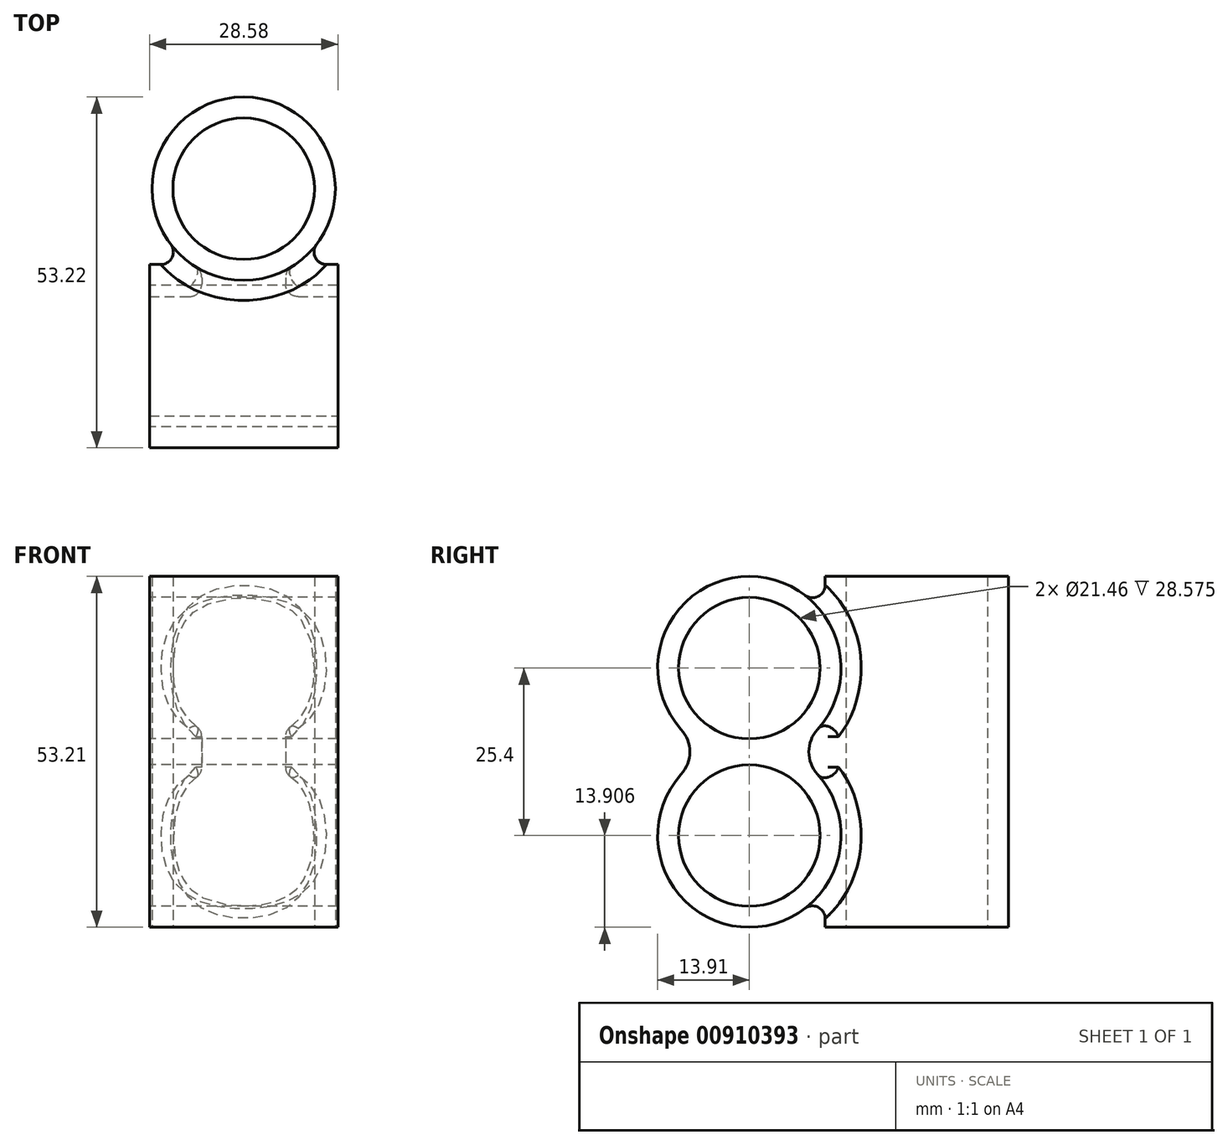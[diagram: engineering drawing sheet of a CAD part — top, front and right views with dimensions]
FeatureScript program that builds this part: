
annotation { "Feature Type Name" : "Feature", "Feature Type Description" : "" }
export const myFeature = defineFeature(function(context is Context, id is Id, definition is map)
    precondition{}
    {
        {
            var Q0;
            Q0=qCreatedBy(makeId("Top.planeOp"),FACE);
            var sketch = newSketch(context, id + "F0", { "sketchPlane" : qUnion([Q0])});
            skCircle(sketch, "E0", {"center": v(0, 0) * mm, "radius": 13.9 * mm});
            skCircle(sketch, "E1", {"center": v(0, 0) * mm, "radius": 10.73 * mm});
            skSolve(sketch);
        }
        {
            var Q0;
            Q0 = qSketchRegion(id + "F0", true);
            extrude(context, id + "F1", {"entities" : qUnion([Q0]), "depth" : 53.2 * mm, "offsetDistance" : 25.4 * mm});
        }
        {
            var Q0;
            Q0=qCreatedBy(makeId("Right.planeOp"),FACE);
            var sketch = newSketch(context, id + "F2", { "sketchPlane" : qUnion([Q0])});
            skCircle(sketch, "E2", {"center": v(-25.4, 13.9) * mm, "radius": 10.73 * mm});
            skCircle(sketch, "E3", {"center": v(-25.4, 39.3) * mm, "radius": 10.73 * mm});
            skArc(sketch, "E4", {"start": v(-31.07, 26.6) * mm, "mid": v(-25.4, 0) * mm, "end": v(-19.73, 26.6) * mm});
            skArc(sketch, "E5", {"start": v(-19.73, 26.6) * mm, "mid": v(-25.4, 53.21) * mm, "end": v(-31.07, 26.6) * mm});
            skSolve(sketch);
        }
        {
            var Q0;
            Q0 = qSketchRegion(id + "F2", true);
            extrude(context, id + "F3", {"entities" : qUnion([Q0]), "operationType" : NewBodyOperationType.ADD, "depth" : 28.57 * mm, "offsetDistance" : 25.4 * mm, "symmetric" : true});
        }
        {
            var Q0;
            {var subQ0=sQuery(id+"F2.wireOp",EDGE,"E5");var subQ1=sQuery(id+"F2.wireOp",EDGE,"E4");Q0=makeQuery(id+"F3.opExtrude","SWEPT_EDGE",EDGE,{"disambiguationData":[OSD([subQ1,subQ0]),TDD([makeQuery(id+"F2.imprint","INTERSECT",VERTEX,{"disambiguationData":[OD(0.0)],"derivedFrom":[subQ1,subQ0]})])]});}
            fillet(context, id + "F4", {"entities" : qUnion([Q0]), "radius" : 5.08 * mm, "tangentPropagation" : true, "allowEdgeOverflow" : false});
        }
        {
            var Q0;
            Q0=qCreatedBy(makeId("Right.planeOp"),FACE);
            var sketch = newSketch(context, id + "F5", { "sketchPlane" : qUnion([Q0])});
            skLineSegment(sketch, "E6", {"start": v(-19.73, 26.6) * mm, "end": v(-11.5, 13.9) * mm});
            skLineSegment(sketch, "E7", {"start": v(-11.5, 13.9) * mm, "end": v(-11.5, 39.3) * mm});
            skLineSegment(sketch, "E8", {"start": v(-11.5, 39.3) * mm, "end": v(-19.73, 26.6) * mm});
            skSolve(sketch);
        }
        {
            var Q0;
            Q0 = qSketchRegion(id + "F5", true);
            extrude(context, id + "F6", {"entities" : qUnion([Q0]), "operationType" : NewBodyOperationType.ADD, "depth" : 12.7 * mm, "offsetDistance" : 25.4 * mm, "symmetric" : true});
        }
        {
            var Q0;
            {var subQ0=sQuery(id+"F2.wireOp",EDGE,"E5");var subQ1=sQuery(id+"F2.wireOp",EDGE,"E4");Q0=makeQuery(id+"F6.boolean.opBoolean","SPLIT",EDGE,{"disambiguationData":[TD([makeQuery(id+"F6.opExtrude","CAP_FACE",FACE,{"disambiguationData":[OSD([sQuery(id+"F5.wireOp",EDGE,"E6"),sQuery(id+"F5.wireOp",EDGE,"E7"),sQuery(id+"F5.wireOp",EDGE,"E8")])],"isStart":false})])],"derivedFrom":makeQuery(id+"F3.opExtrude","SWEPT_EDGE",EDGE,{"disambiguationData":[OSD([subQ1,subQ0]),TDD([makeQuery(id+"F2.imprint","INTERSECT",VERTEX,{"disambiguationData":[OD(1.0)],"derivedFrom":[subQ1,subQ0]})])]})});}
            var Q1;
            {var subQ0=sQuery(id+"F2.wireOp",EDGE,"E5");var subQ1=sQuery(id+"F2.wireOp",EDGE,"E4");Q1=makeQuery(id+"F6.boolean.opBoolean","SPLIT",EDGE,{"disambiguationData":[TD([makeQuery(id+"F6.opExtrude","CAP_FACE",FACE,{"disambiguationData":[OSD([sQuery(id+"F5.wireOp",EDGE,"E6"),sQuery(id+"F5.wireOp",EDGE,"E7"),sQuery(id+"F5.wireOp",EDGE,"E8")])],"isStart":true})])],"derivedFrom":makeQuery(id+"F3.opExtrude","SWEPT_EDGE",EDGE,{"disambiguationData":[OSD([subQ1,subQ0]),TDD([makeQuery(id+"F2.imprint","INTERSECT",VERTEX,{"disambiguationData":[OD(1.0)],"derivedFrom":[subQ1,subQ0]})])]})});}
            fillet(context, id + "F7", {"entities" : qUnion([Q0, Q1]), "radius" : 5.08 * mm, "tangentPropagation" : true, "allowEdgeOverflow" : false});
        }
        {
            var Q0;
            Q0=makeQuery(id+"F3.boolean.opBoolean","INTERSECT",EDGE,{"derivedFrom":[makeQuery(id+"F1.opExtrude","SWEPT_FACE",FACE,{"disambiguationData":[OSD([sQuery(id+"F0.wireOp",EDGE,"E0")])]}),makeQuery(id+"F3.opExtrude","SWEPT_FACE",FACE,{"disambiguationData":[OSD([sQuery(id+"F2.wireOp",EDGE,"E4")])]})]});
            var Q1;
            Q1=makeQuery(id+"F3.boolean.opBoolean","INTERSECT",EDGE,{"derivedFrom":[makeQuery(id+"F1.opExtrude","SWEPT_FACE",FACE,{"disambiguationData":[OSD([sQuery(id+"F0.wireOp",EDGE,"E0")])]}),makeQuery(id+"F3.opExtrude","SWEPT_FACE",FACE,{"disambiguationData":[OSD([sQuery(id+"F2.wireOp",EDGE,"E5")])]})]});
            var Q2;
            {var subQ0=makeQuery(id+"F6.opExtrude","CAP_FACE",FACE,{"disambiguationData":[OSD([sQuery(id+"F5.wireOp",EDGE,"E6"),sQuery(id+"F5.wireOp",EDGE,"E7"),sQuery(id+"F5.wireOp",EDGE,"E8")])],"isStart":false});var subQ1=sQuery(id+"F2.wireOp",EDGE,"E5");var subQ2=sQuery(id+"F2.wireOp",EDGE,"E4");Q2=makeQuery(id+"F7.opFillet","BLEND_EDGE",EDGE,{"blendedFrom":[makeQuery(id+"F6.boolean.opBoolean","SPLIT",EDGE,{"disambiguationData":[TD([subQ0])],"derivedFrom":makeQuery(id+"F3.opExtrude","SWEPT_EDGE",EDGE,{"disambiguationData":[OSD([subQ2,subQ1]),TDD([makeQuery(id+"F2.imprint","INTERSECT",VERTEX,{"disambiguationData":[OD(1.0)],"derivedFrom":[subQ2,subQ1]})])]})}),subQ0],"blendedInto":[subQ0]});}
            var Q3;
            Q3=makeQuery(id+"F6.boolean.opBoolean","INTERSECT",EDGE,{"derivedFrom":[makeQuery(id+"F3.opExtrude","SWEPT_FACE",FACE,{"disambiguationData":[OSD([sQuery(id+"F2.wireOp",EDGE,"E5")])]}),makeQuery(id+"F6.opExtrude","CAP_FACE",FACE,{"disambiguationData":[OSD([sQuery(id+"F5.wireOp",EDGE,"E6"),sQuery(id+"F5.wireOp",EDGE,"E7"),sQuery(id+"F5.wireOp",EDGE,"E8")])],"isStart":false})]});
            var Q4;
            Q4=makeQuery(id+"F6.boolean.opBoolean","INTERSECT",EDGE,{"derivedFrom":[makeQuery(id+"F3.opExtrude","SWEPT_FACE",FACE,{"disambiguationData":[OSD([sQuery(id+"F2.wireOp",EDGE,"E4")])]}),makeQuery(id+"F6.opExtrude","CAP_FACE",FACE,{"disambiguationData":[OSD([sQuery(id+"F5.wireOp",EDGE,"E6"),sQuery(id+"F5.wireOp",EDGE,"E7"),sQuery(id+"F5.wireOp",EDGE,"E8")])],"isStart":false})]});
            var Q5;
            Q5=makeQuery(id+"F6.boolean.opBoolean","INTERSECT",EDGE,{"derivedFrom":[makeQuery(id+"F1.opExtrude","SWEPT_FACE",FACE,{"disambiguationData":[OSD([sQuery(id+"F0.wireOp",EDGE,"E0")])]}),makeQuery(id+"F6.opExtrude","CAP_FACE",FACE,{"disambiguationData":[OSD([sQuery(id+"F5.wireOp",EDGE,"E6"),sQuery(id+"F5.wireOp",EDGE,"E7"),sQuery(id+"F5.wireOp",EDGE,"E8")])],"isStart":false})]});
            var Q6;
            Q6=makeQuery(id+"F6.boolean.opBoolean","INTERSECT",EDGE,{"derivedFrom":[makeQuery(id+"F1.opExtrude","SWEPT_FACE",FACE,{"disambiguationData":[OSD([sQuery(id+"F0.wireOp",EDGE,"E0")])]}),makeQuery(id+"F6.opExtrude","CAP_FACE",FACE,{"disambiguationData":[OSD([sQuery(id+"F5.wireOp",EDGE,"E6"),sQuery(id+"F5.wireOp",EDGE,"E7"),sQuery(id+"F5.wireOp",EDGE,"E8")])],"isStart":true})]});
            var Q7;
            Q7=makeQuery(id+"F6.boolean.opBoolean","INTERSECT",EDGE,{"derivedFrom":[makeQuery(id+"F3.opExtrude","SWEPT_FACE",FACE,{"disambiguationData":[OSD([sQuery(id+"F2.wireOp",EDGE,"E5")])]}),makeQuery(id+"F6.opExtrude","CAP_FACE",FACE,{"disambiguationData":[OSD([sQuery(id+"F5.wireOp",EDGE,"E6"),sQuery(id+"F5.wireOp",EDGE,"E7"),sQuery(id+"F5.wireOp",EDGE,"E8")])],"isStart":true})]});
            var Q8;
            {var subQ0=makeQuery(id+"F6.opExtrude","CAP_FACE",FACE,{"disambiguationData":[OSD([sQuery(id+"F5.wireOp",EDGE,"E6"),sQuery(id+"F5.wireOp",EDGE,"E7"),sQuery(id+"F5.wireOp",EDGE,"E8")])],"isStart":true});var subQ1=sQuery(id+"F2.wireOp",EDGE,"E5");var subQ2=sQuery(id+"F2.wireOp",EDGE,"E4");Q8=makeQuery(id+"F7.opFillet","BLEND_EDGE",EDGE,{"blendedFrom":[makeQuery(id+"F6.boolean.opBoolean","SPLIT",EDGE,{"disambiguationData":[TD([subQ0])],"derivedFrom":makeQuery(id+"F3.opExtrude","SWEPT_EDGE",EDGE,{"disambiguationData":[OSD([subQ2,subQ1]),TDD([makeQuery(id+"F2.imprint","INTERSECT",VERTEX,{"disambiguationData":[OD(1.0)],"derivedFrom":[subQ2,subQ1]})])]})}),subQ0],"blendedInto":[subQ0]});}
            var Q9;
            Q9=makeQuery(id+"F6.boolean.opBoolean","INTERSECT",EDGE,{"derivedFrom":[makeQuery(id+"F3.opExtrude","SWEPT_FACE",FACE,{"disambiguationData":[OSD([sQuery(id+"F2.wireOp",EDGE,"E4")])]}),makeQuery(id+"F6.opExtrude","CAP_FACE",FACE,{"disambiguationData":[OSD([sQuery(id+"F5.wireOp",EDGE,"E6"),sQuery(id+"F5.wireOp",EDGE,"E7"),sQuery(id+"F5.wireOp",EDGE,"E8")])],"isStart":true})]});
            fillet(context, id + "F8", {"entities" : qUnion([Q0, Q1, Q2, Q3, Q4, Q5, Q6, Q7, Q8, Q9]), "radius" : 1.9 * mm, "tangentPropagation" : true, "allowEdgeOverflow" : false});
        }
    });
